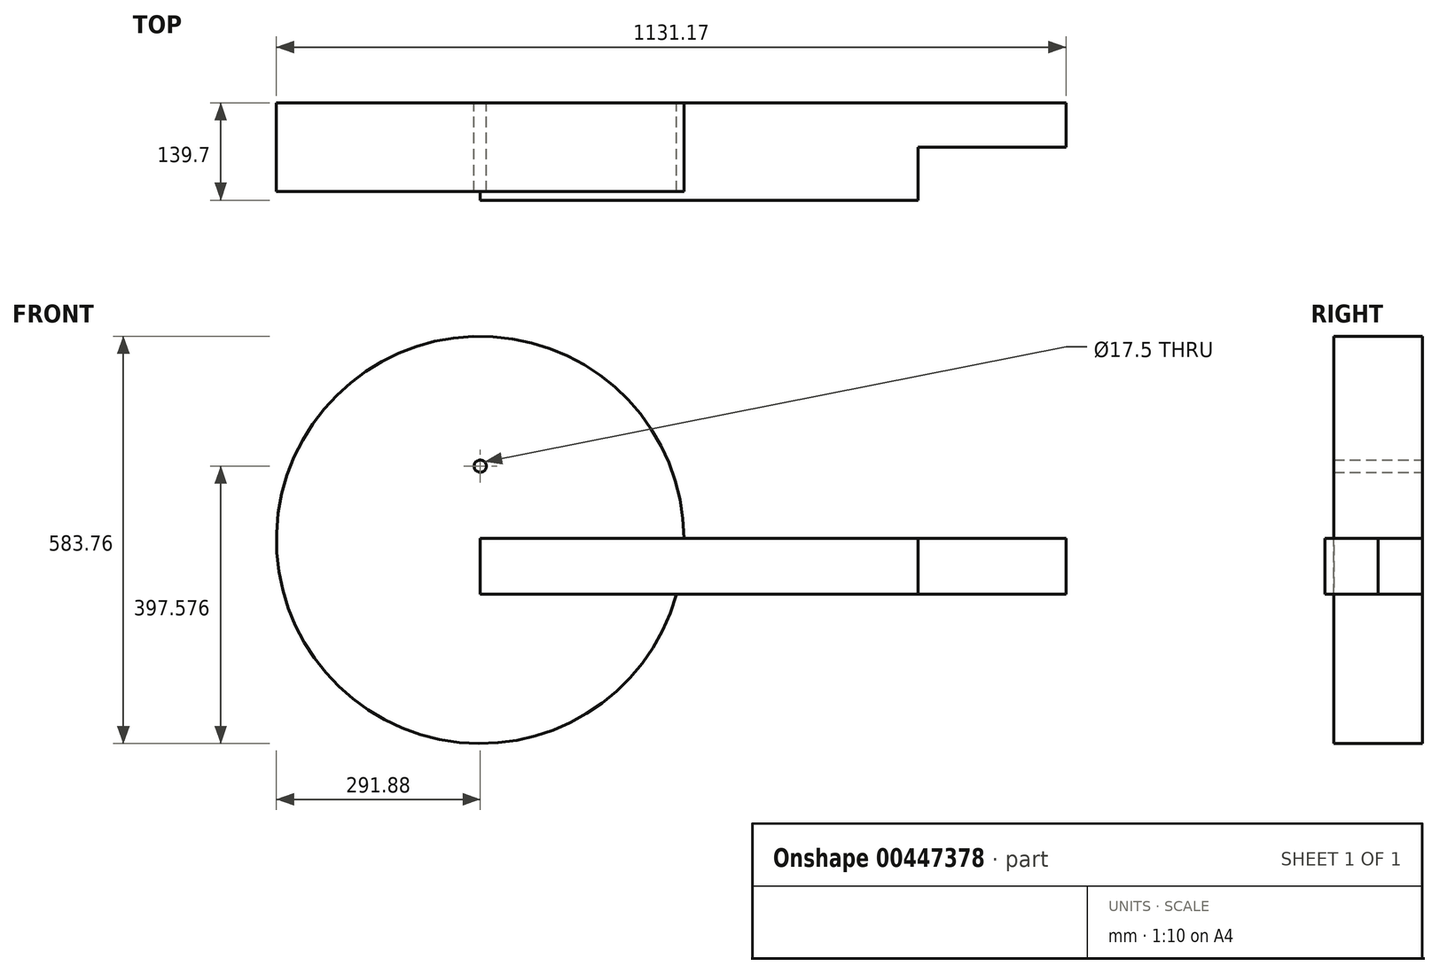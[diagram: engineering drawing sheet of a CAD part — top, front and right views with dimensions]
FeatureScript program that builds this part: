
annotation { "Feature Type Name" : "Feature", "Feature Type Description" : "" }
export const myFeature = defineFeature(function(context is Context, id is Id, definition is map)
    precondition{}
    {
        {
            var Q0;
            Q0=qCreatedBy(makeId("Front.planeOp"),FACE);
            var sketch = newSketch(context, id + "F0", { "sketchPlane" : qUnion([Q0])});
            skLineSegment(sketch, "E0.bottom", {"start": v(0, 218.92) * mm, "end": v(627.07, 218.92) * mm});
            skLineSegment(sketch, "E0.top", {"start": v(0, 298.96) * mm, "end": v(627.07, 298.96) * mm});
            skLineSegment(sketch, "E0.left", {"start": v(0, 218.92) * mm, "end": v(0, 298.96) * mm});
            skLineSegment(sketch, "E0.right", {"start": v(627.07, 218.92) * mm, "end": v(627.07, 298.96) * mm});
            skSolve(sketch);
        }
        {
            var Q0;
            Q0 = qSketchRegion(id + "F0", true);
            var sketch = newSketch(context, id + "F1", { "sketchPlane" : qUnion([Q0])});
            skCircle(sketch, "E1", {"center": v(0, 296.86) * mm, "radius": 291.88 * mm});
            skSolve(sketch);
        }
        {
            var Q0;
            {var subQ5=makeQuery(id+"F0.imprint","IMPRINT",EDGE,{"derivedFrom":sQuery(id+"F0.wireOp",EDGE,"E0.left")});Q0=makeQuery(id+"F1.imprint","IMPRINT",FACE,{"disambiguationData":[TD([[makeQuery(id+"F1.imprint","IMPRINT",EDGE,{"derivedFrom":subQ5}),1.0]])]});}
            extrude(context, id + "F2", {"entities" : qUnion([Q0]), "endBound" : BoundingType.SYMMETRIC, "depth" : 127 * mm});
        }
        {
            var Q0;
            Q0 = qSketchRegion(id + "F0", true);
            var Q1;
            Q1=makeQuery(id+"F0.imprint","IMPRINT",FACE,{"disambiguationData":[TD([[makeQuery(id+"F0.imprint","IMPRINT",EDGE,{"derivedFrom":sQuery(id+"F0.wireOp",EDGE,"E0.bottom")}),1.0]])]});
            extrude(context, id + "F3", {"entities" : qUnion([Q0, Q1]), "operationType" : NewBodyOperationType.ADD, "depth" : 76.2 * mm});
        }
        {
            var Q0;
            Q0=makeQuery(id+"F2.opExtrude","CAP_FACE",FACE,{"disambiguationData":[OSD([sQuery(id+"F0.wireOp",EDGE,"E0.bottom"),sQuery(id+"F0.wireOp",EDGE,"E0.top"),sQuery(id+"F0.wireOp",EDGE,"E0.left"),sQuery(id+"F1.wireOp",EDGE,"E1")])],"isStart":true});
            var sketch = newSketch(context, id + "F4", { "sketchPlane" : qUnion([Q0])});
            skCircle(sketch, "E2", {"center": v(0, 402.56) * mm, "radius": 60.6 * mm});
            skSolve(sketch);
        }
        {
            var Q0;
            Q0=sQuery(id+"F4.wireOp",VERTEX,"E2.center");
            var Q1;
            Q1=makeQuery(id+"F2.opExtrude","SWEPT_BODY",BODY,{"disambiguationData":[OSD([sQuery(id+"F0.wireOp",EDGE,"E0.bottom"),sQuery(id+"F0.wireOp",EDGE,"E0.top"),sQuery(id+"F0.wireOp",EDGE,"E0.left"),sQuery(id+"F1.wireOp",EDGE,"E1")])]});
            hole(context, id + "F5", {"style" : HoleStyle.SIMPLE, "endStyle" : HoleEndStyle.THROUGH, "standardTappedOrClearance" : lookupTablePath({ "fit" : "Normal", "standard" : "ISO", "engagement" : "75%", "pitch" : "2.5 mm", "size" : "M20", "type" : "Tapped" }), "standardBlindInLast" : lookupTablePath({ "fit" : "Standard", "standard" : "ISO", "engagement" : "75%", "pitch" : "2.5 mm", "size" : "M20", "type" : "Tapped" }), "holeDiameter" : 17.5 * mm, "showTappedDepth" : true, "isTappedThrough" : true, "tappedDepth" : 12.7 * mm, "tapClearance" : 3, "locations" : qUnion([Q0]), "scope" : qUnion([Q1]), "majorDiameter" : 20 * mm});
        }
        {
            var Q0;
            Q0=makeQuery(id+"F2.opExtrude","SWEPT_FACE",FACE,{"disambiguationData":[OSD([sQuery(id+"F0.wireOp",EDGE,"E0.left")])]});
            var sketch = newSketch(context, id + "F6", { "sketchPlane" : qUnion([Q0])});
            skSolve(sketch);
        }
        {
            var Q0;
            {var subQ0=sQuery(id+"F0.wireOp",EDGE,"E0.left");Q0=makeQuery(id+"F6.imprint","IMPRINT",FACE,{"disambiguationData":[TD([[makeQuery(id+"F6.imprint","IMPRINT",EDGE,{"derivedFrom":makeQuery(id+"F2.opExtrude","CAP_EDGE",EDGE,{"disambiguationData":[OSD([subQ0])],"isStart":true})}),1.0]])]});}
            extrude(context, id + "F7", {"entities" : qUnion([Q0]), "operationType" : NewBodyOperationType.ADD, "depth" : 839.3 * mm});
        }
    });
